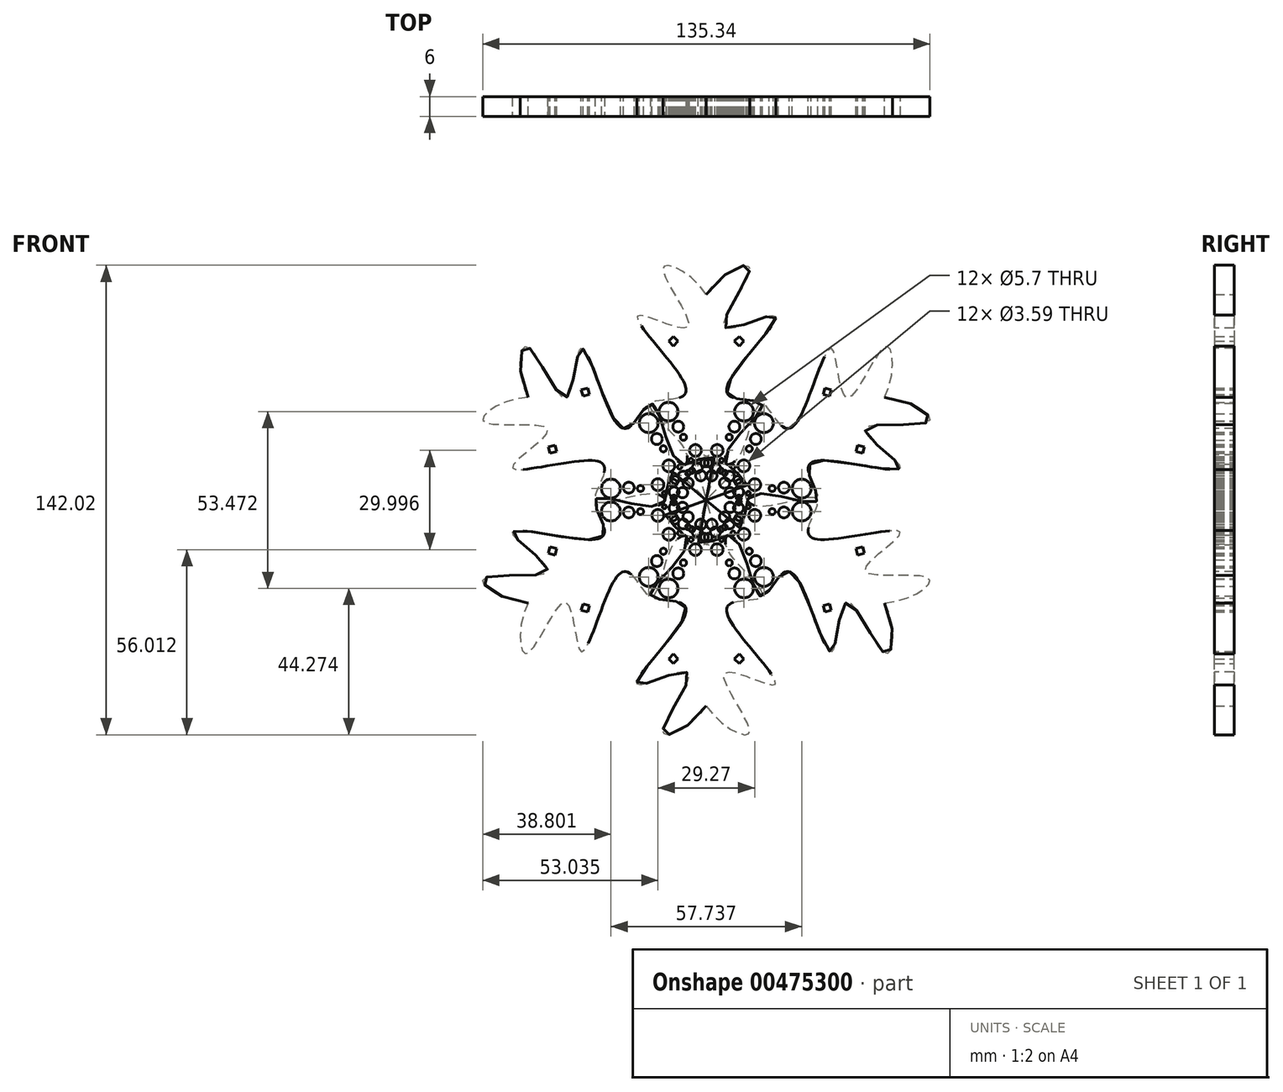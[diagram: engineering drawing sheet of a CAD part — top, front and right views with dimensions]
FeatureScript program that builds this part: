
annotation { "Feature Type Name" : "Feature", "Feature Type Description" : "" }
export const myFeature = defineFeature(function(context is Context, id is Id, definition is map)
    precondition{}
    {
        {
            var Q0;
            Q0=qCreatedBy(makeId("Front.planeOp"),FACE);
            var sketch = newSketch(context, id + "F0", { "sketchPlane" : qUnion([Q0])});
            skLineSegment(sketch, "E0", {"start": v(0, 0) * mm, "end": v(0, 67.48) * mm, "construction": true});
            skFitSpline(sketch, "E1", {"points": [v(0, 62.23) * mm, v(13.12, 70.1) * mm, v(5.54, 52.32) * mm, v(20.7, 55.82) * mm, v(7.29, 36.58) * mm, v(7.87, 31.04) * mm, v(16.9, 29) * mm, v(8.16, 17.63) * mm, v(7.58, 9.18) * mm, v(0, 0) * mm], "startDerivative": vector(102.18, 160.57) * mm, "endDerivative": vector(-567.06, -125.56) * mm});
            skCircle(sketch, "E2", {"center": v(5.54, 5.13) * mm, "radius": 1.57 * mm});
            skCircle(sketch, "E3", {"center": v(2.76, 9.66) * mm, "radius": 1.52 * mm});
            skCircle(sketch, "E4", {"center": v(3.3, 15) * mm, "radius": 1.8 * mm});
            skCircle(sketch, "E5", {"center": v(6.93, 19) * mm, "radius": 0.93 * mm});
            skCircle(sketch, "E6", {"center": v(8.5, 22.2) * mm, "radius": 1.65 * mm});
            skCircle(sketch, "E7", {"center": v(11.43, 26.74) * mm, "radius": 2.85 * mm});
            skCircle(sketch, "E8", {"center": v(10.01, 5.13) * mm, "radius": 1.17 * mm});
            skCircle(sketch, "E9", {"center": v(5.54, 8.2) * mm, "radius": 0.8 * mm});
            skCircle(sketch, "E10", {"center": v(4.6, 12) * mm, "radius": 0.62 * mm});
            skLineSegment(sketch, "E11.bottom", {"start": v(9.93, 49.43) * mm, "end": v(11.34, 48.02) * mm});
            skLineSegment(sketch, "E11.top", {"start": v(8.51, 48.02) * mm, "end": v(9.93, 46.6) * mm});
            skLineSegment(sketch, "E11.left", {"start": v(9.93, 49.43) * mm, "end": v(8.51, 48.02) * mm});
            skLineSegment(sketch, "E11.right", {"start": v(11.34, 48.02) * mm, "end": v(9.93, 46.6) * mm});
            skLineSegment(sketch, "E12.MirrorCS", {"start": v(-9.93, 49.43) * mm, "end": v(-8.51, 48.02) * mm});
            skLineSegment(sketch, "E13.MirrorCS", {"start": v(-11.34, 48.02) * mm, "end": v(-9.93, 46.6) * mm});
            skLineSegment(sketch, "E14.MirrorCS", {"start": v(-8.51, 48.02) * mm, "end": v(-9.93, 46.6) * mm});
            skLineSegment(sketch, "E15.MirrorCS", {"start": v(-9.93, 49.43) * mm, "end": v(-11.34, 48.02) * mm});
            skCircle(sketch, "E16.MirrorC", {"center": v(-5.54, 5.13) * mm, "radius": 1.57 * mm});
            skCircle(sketch, "E17.MirrorC", {"center": v(-2.76, 9.66) * mm, "radius": 1.52 * mm});
            skCircle(sketch, "E18.MirrorC", {"center": v(-3.3, 15) * mm, "radius": 1.8 * mm});
            skCircle(sketch, "E19.MirrorC", {"center": v(-6.93, 19) * mm, "radius": 0.93 * mm});
            skCircle(sketch, "E20.MirrorC", {"center": v(-8.5, 22.2) * mm, "radius": 1.65 * mm});
            skCircle(sketch, "E21.MirrorC", {"center": v(-10.01, 5.13) * mm, "radius": 1.17 * mm});
            skCircle(sketch, "E22.MirrorC", {"center": v(-5.54, 8.2) * mm, "radius": 0.8 * mm});
            skCircle(sketch, "E23.MirrorC", {"center": v(-4.6, 12) * mm, "radius": 0.62 * mm});
            skFitSpline(sketch, "E24.MirrorCS", {"points": [v(0, 62.23) * mm, v(-13.12, 70.1) * mm, v(-5.54, 52.32) * mm, v(-20.7, 55.82) * mm, v(-7.29, 36.58) * mm, v(-7.87, 31.04) * mm, v(-16.9, 29) * mm, v(-8.16, 17.63) * mm, v(-7.58, 9.18) * mm, v(0, 0) * mm], "startDerivative": vector(-102.18, 160.57) * mm, "endDerivative": vector(567.06, -125.56) * mm});
            skCircle(sketch, "E25.MirrorC", {"center": v(-11.43, 26.74) * mm, "radius": 2.85 * mm});
            skSolve(sketch);
        }
        {
            var Q0;
            Q0 = qSketchRegion(id + "F0", true);
            extrude(context, id + "F1", {"entities" : qUnion([Q0]), "depth" : 6 * mm});
        }
        {
            var Q0;
            Q0=qCreatedBy(makeId("Right.planeOp"),FACE);
            var sketch = newSketch(context, id + "F2", { "sketchPlane" : qUnion([Q0])});
            skLineSegment(sketch, "E26", {"start": v(0, 0) * mm, "end": v(-58.6, 0) * mm, "construction": true});
            skSolve(sketch);
        }
        {
            var Q0;
            Q0=makeQuery(id+"F1.opExtrude","SWEPT_BODY",BODY,{"disambiguationData":[OSD([sQuery(id+"F0.wireOp",EDGE,"E1"),sQuery(id+"F0.wireOp",EDGE,"E2"),sQuery(id+"F0.wireOp",EDGE,"E3"),sQuery(id+"F0.wireOp",EDGE,"E4"),sQuery(id+"F0.wireOp",EDGE,"E5"),sQuery(id+"F0.wireOp",EDGE,"E6"),sQuery(id+"F0.wireOp",EDGE,"E7"),sQuery(id+"F0.wireOp",EDGE,"E8"),sQuery(id+"F0.wireOp",EDGE,"E9"),sQuery(id+"F0.wireOp",EDGE,"E10"),sQuery(id+"F0.wireOp",EDGE,"E11.right"),sQuery(id+"F0.wireOp",EDGE,"E12.MirrorCS"),sQuery(id+"F0.wireOp",EDGE,"E13.MirrorCS"),sQuery(id+"F0.wireOp",EDGE,"E11.left"),sQuery(id+"F0.wireOp",EDGE,"E11.top"),sQuery(id+"F0.wireOp",EDGE,"E11.bottom"),sQuery(id+"F0.wireOp",EDGE,"E15.MirrorCS"),sQuery(id+"F0.wireOp",EDGE,"E14.MirrorCS"),sQuery(id+"F0.wireOp",EDGE,"E16.MirrorC"),sQuery(id+"F0.wireOp",EDGE,"E17.MirrorC"),sQuery(id+"F0.wireOp",EDGE,"E18.MirrorC"),sQuery(id+"F0.wireOp",EDGE,"E19.MirrorC"),sQuery(id+"F0.wireOp",EDGE,"E20.MirrorC"),sQuery(id+"F0.wireOp",EDGE,"E21.MirrorC"),sQuery(id+"F0.wireOp",EDGE,"E22.MirrorC"),sQuery(id+"F0.wireOp",EDGE,"E23.MirrorC"),sQuery(id+"F0.wireOp",EDGE,"E24.MirrorCS"),sQuery(id+"F0.wireOp",EDGE,"E25.MirrorC")])]});
            var Q1;
            Q1=sQuery(id+"F2.wireOp",EDGE,"E26");
            circularPattern(context, id + "F3", {"entities" : qUnion([Q0]), "axis" : qUnion([Q1]), "angle" : 360 * degree, "instanceCount" : 6, "equalSpace" : true});
        }
    });
